# Revit family: Sink-Pedestal-KOHLER-Memoirs-K-2238
name_source: partatom
category: Plumbing Fixtures
units: mm (PartAtom-declared; Revit-internal decimal feet)

## family parameters
Cut with Voids When Loaded = No
Host = Face
OmniClass Number = 23.31.13.00
Part Type = Normal
Room Calculation Point = No
Round Connector Dimension = Use Diameter
Shared = No

## types (1)
- Not a Type - See Type Catalog
    ADA Compliant = No
    Assembly Code = D2010400
    Center Hole = No
    Centerset = No
    Cold Water Inlet = Cold Water Inlet
    Date Modified = 04/03/2019
    Default Elevation = 0"
    Description = Classic 24 inch pedestal bathroom sink with 8 inch widespread faucet holes
    Drain Included = No
    Faucet Hole Spacing = 8"
    Finish = Default
    Height = 34 3/8"
    Hot Water Inlet = Hot Water Inlet
    Length = 24 3/16"
    Manufacturer = KOHLER Co.
    MasterFormat 1995 = 15410
    MasterFormat 2004 = 22.41.16
    Material = Fireclay
    Model = K-2338-8-7
    Product Documentation Link = https://www.us.kohler.com
    Product Name = Memoirs
    Product Page URL = http://www.us.kohler.com
    Product data url = https://www.bimobject.com
    Type = 27
    URL = https://www.us.kohler.com
    Vent Connection = No
    Waste Connection = Yes
    Waste Water Outlet = Waste Water Outlet
    WaterSense Certified = No
    Widespread = Yes
    Width = 19 7/8"

## geometry (parser evidence)
native form markers: Sweep x2
no freeform markers — native parametric forms only
